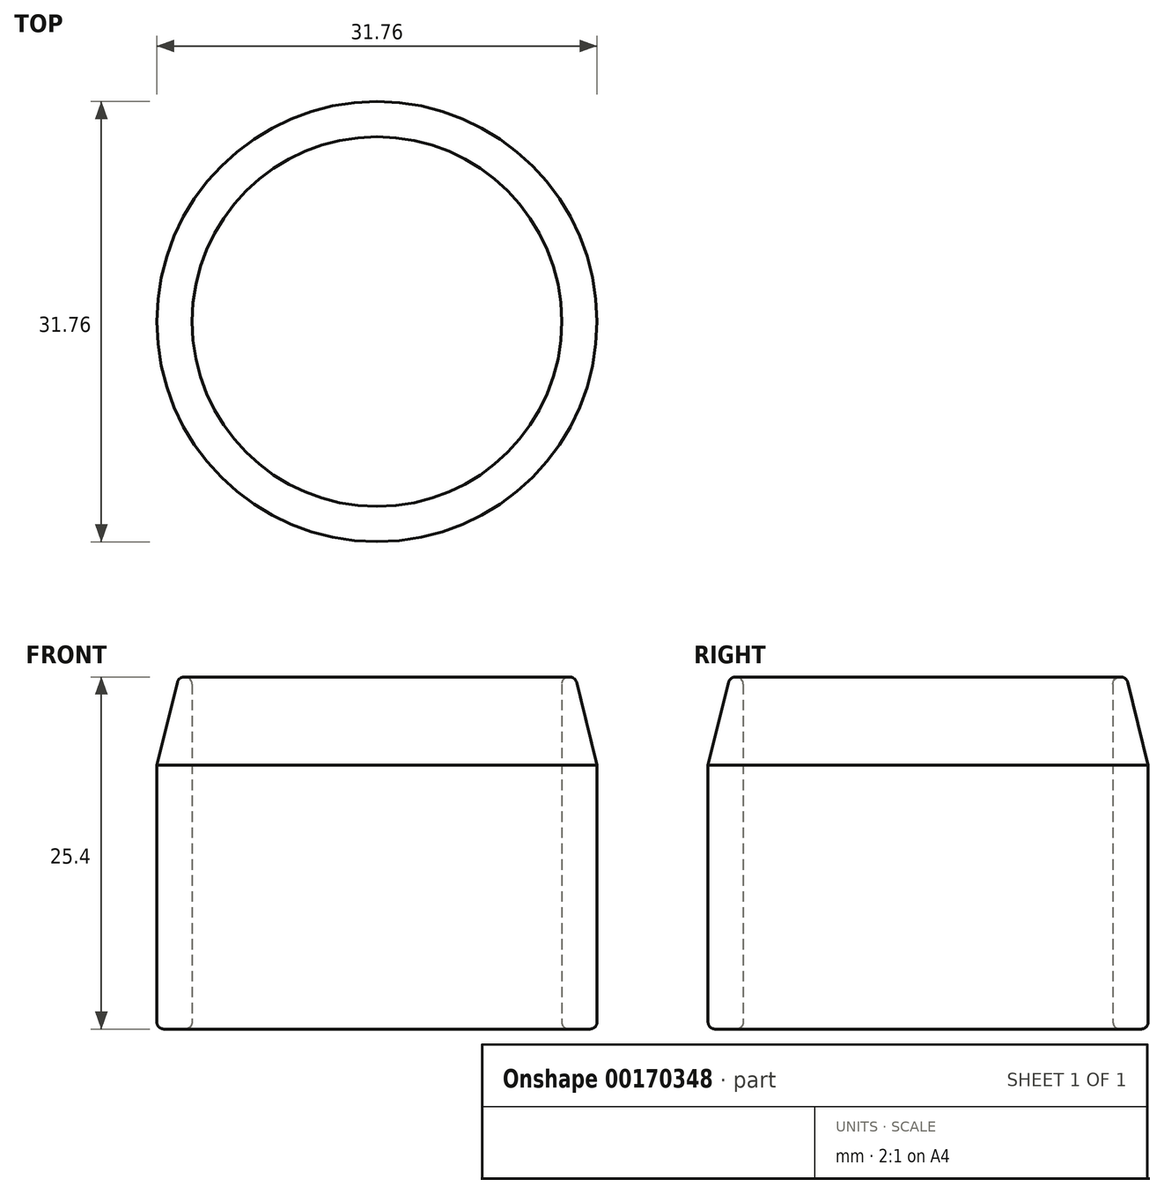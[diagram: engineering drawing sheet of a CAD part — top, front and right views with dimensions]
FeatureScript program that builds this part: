
annotation { "Feature Type Name" : "Feature", "Feature Type Description" : "" }
export const myFeature = defineFeature(function(context is Context, id is Id, definition is map)
    precondition{}
    {
        {
            var Q0;
            Q0=qCreatedBy(makeId("Top.planeOp"),FACE);
            var sketch = newSketch(context, id + "F0", { "sketchPlane" : qUnion([Q0])});
            skCircle(sketch, "E0", {"center": v(0, 0) * mm, "radius": 13.34 * mm});
            skCircle(sketch, "E1", {"center": v(0, 0) * mm, "radius": 15.88 * mm});
            skSolve(sketch);
        }
        {
            var Q0;
            Q0=makeQuery(id+"F0.imprint","IMPRINT",FACE,{"disambiguationData":[TD([[makeQuery(id+"F0.imprint","IMPRINT",EDGE,{"derivedFrom":sQuery(id+"F0.wireOp",EDGE,"E0")}),-1.0]])]});
            extrude(context, id + "F1", {"entities" : qUnion([Q0]), "depth" : 25.4 * mm});
        }
        {
            var Q0;
            Q0=makeQuery(id+"F1.opExtrude","CAP_EDGE",EDGE,{"disambiguationData":[OSD([sQuery(id+"F0.wireOp",EDGE,"E1")])],"isStart":false});
            chamfer(context, id + "F2", {"entities" : qUnion([Q0]), "chamferType" : ChamferType.TWO_OFFSETS, "width1" : 6.35 * mm, "oppositeDirection" : true, "width2" : 1.57 * mm, "tangentPropagation" : true});
        }
        {
            var Q0;
            {var subQ0=sQuery(id+"F0.wireOp",EDGE,"E1");Q0=makeQuery(id+"F2.opChamfer","BLEND_EDGE",EDGE,{"blendedFrom":[makeQuery(id+"F1.opExtrude","CAP_EDGE",EDGE,{"disambiguationData":[OSD([subQ0])],"isStart":false}),makeQuery(id+"F1.opExtrude","CAP_FACE",FACE,{"disambiguationData":[OSD([sQuery(id+"F0.wireOp",EDGE,"E0"),subQ0])],"isStart":false})],"blendedInto":[makeQuery(id+"F1.opExtrude","CAP_FACE",FACE,{"disambiguationData":[OSD([sQuery(id+"F0.wireOp",EDGE,"E0"),subQ0])],"isStart":false})]});}
            var Q1;
            Q1=makeQuery(id+"F1.opExtrude","CAP_EDGE",EDGE,{"disambiguationData":[OSD([sQuery(id+"F0.wireOp",EDGE,"E0")])],"isStart":false});
            var Q2;
            Q2=makeQuery(id+"F1.opExtrude","CAP_EDGE",EDGE,{"disambiguationData":[OSD([sQuery(id+"F0.wireOp",EDGE,"E1")])],"isStart":true});
            var Q3;
            Q3=makeQuery(id+"F1.opExtrude","CAP_EDGE",EDGE,{"disambiguationData":[OSD([sQuery(id+"F0.wireOp",EDGE,"E0")])],"isStart":true});
            fillet(context, id + "F3", {"entities" : qUnion([Q0, Q1, Q2, Q3]), "radius" : 0.5 * mm, "tangentPropagation" : true, "allowEdgeOverflow" : false});
        }
    });
